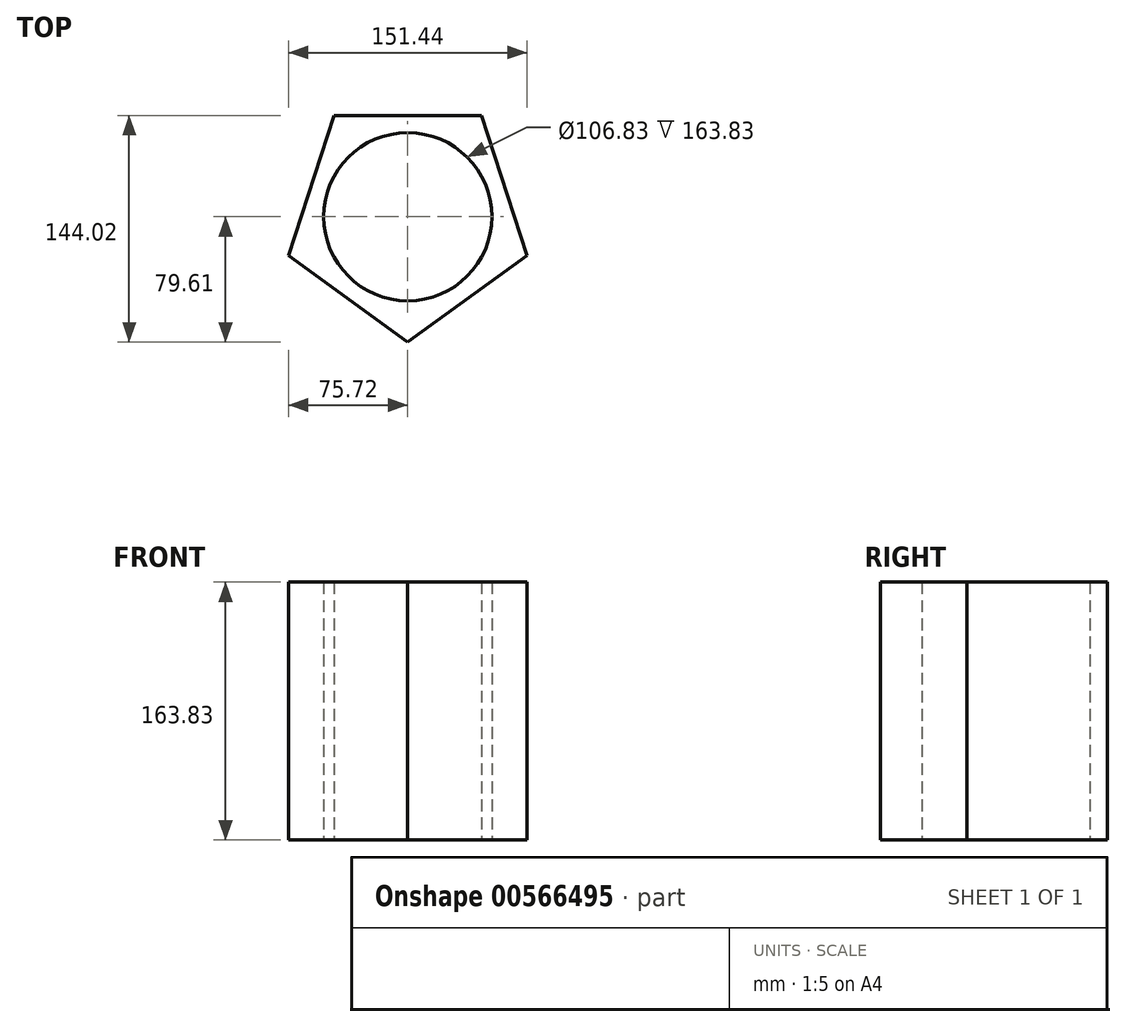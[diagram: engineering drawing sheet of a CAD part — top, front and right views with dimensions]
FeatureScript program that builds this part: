
annotation { "Feature Type Name" : "Feature", "Feature Type Description" : "" }
export const myFeature = defineFeature(function(context is Context, id is Id, definition is map)
    precondition{}
    {
        {
            var Q0;
            Q0=qCreatedBy(makeId("Top.planeOp"),FACE);
            var sketch = newSketch(context, id + "F0", { "sketchPlane" : qUnion([Q0])});
            skCircle(sketch, "E0.cCircle", {"center": v(0, 0) * mm, "radius": 64.4 * mm, "construction": true});
            skLineSegment(sketch, "E0.0", {"start": v(-46.8, 64.4) * mm, "end": v(46.8, 64.4) * mm});
            skLineSegment(sketch, "E0.1", {"start": v(46.8, 64.4) * mm, "end": v(75.72, -24.6) * mm});
            skLineSegment(sketch, "E0.2", {"start": v(75.72, -24.6) * mm, "end": v(0, -79.61) * mm});
            skLineSegment(sketch, "E0.3", {"start": v(0, -79.61) * mm, "end": v(-75.72, -24.6) * mm});
            skLineSegment(sketch, "E0.4", {"start": v(-75.72, -24.6) * mm, "end": v(-46.8, 64.4) * mm});
            skPoint(sketch, "E0.0.midPoint", {"position": v(0, 64.4) * mm});
            skCircle(sketch, "E1", {"center": v(0, 0) * mm, "radius": 53.41 * mm});
            skSolve(sketch);
        }
        {
            var Q0;
            Q0 = qSketchRegion(id + "F0", true);
            extrude(context, id + "F1", {"entities" : qUnion([Q0]), "depth" : 163.83 * mm, "offsetDistance" : 25.4 * mm});
        }
    });
